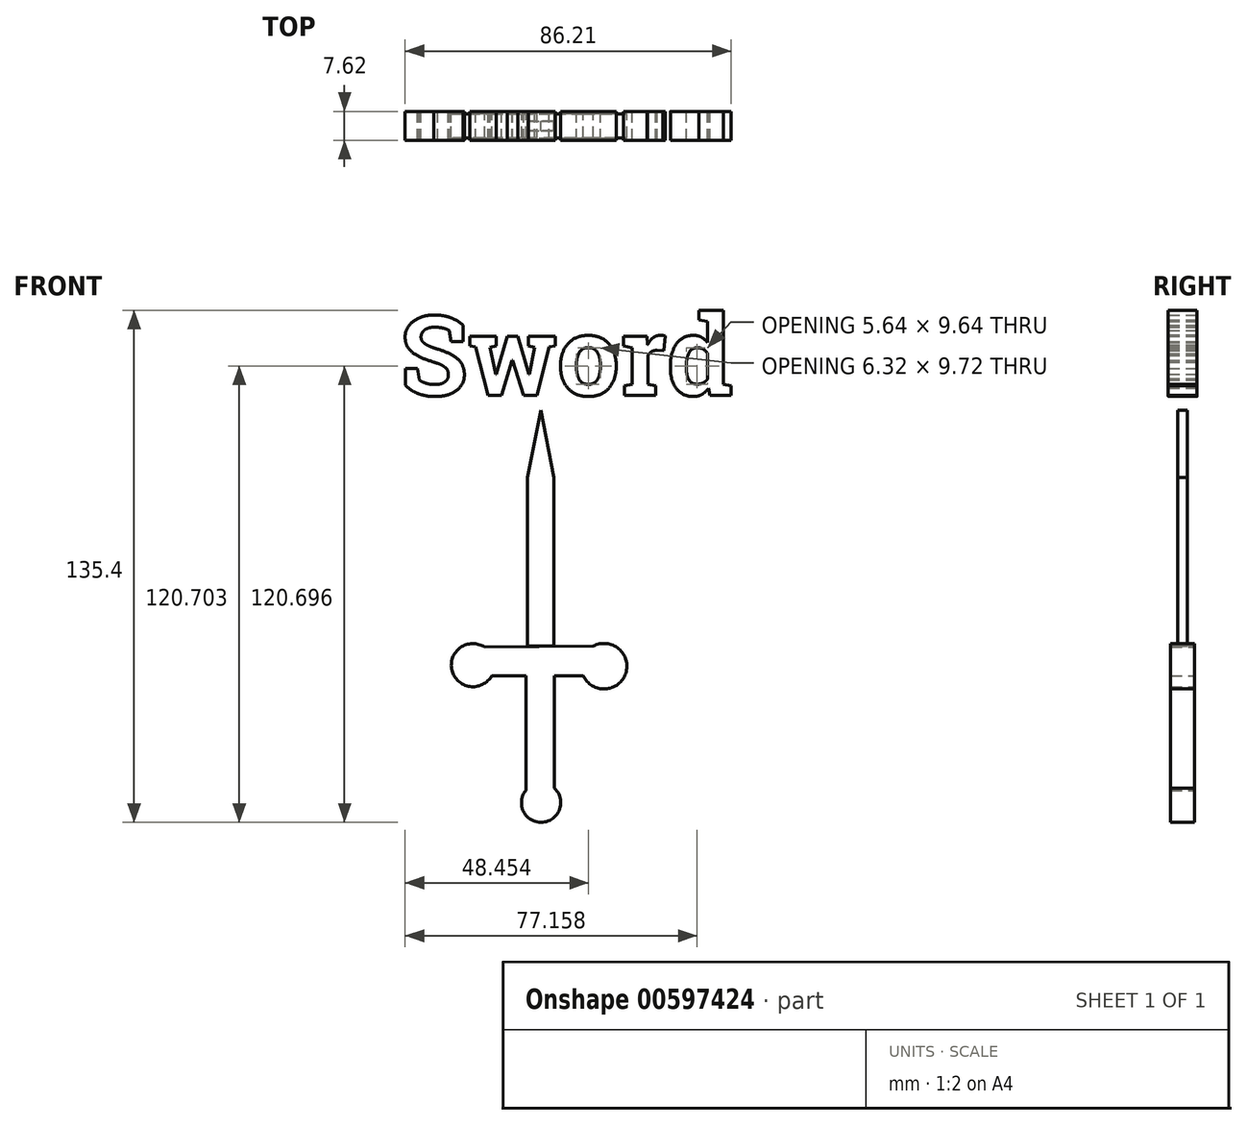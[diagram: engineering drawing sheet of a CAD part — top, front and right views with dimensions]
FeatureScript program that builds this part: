
annotation { "Feature Type Name" : "Feature", "Feature Type Description" : "" }
export const myFeature = defineFeature(function(context is Context, id is Id, definition is map)
    precondition{}
    {
        {
            var Q0;
            Q0=qCreatedBy(makeId("Front.planeOp"),FACE);
            var sketch = newSketch(context, id + "F0", { "sketchPlane" : qUnion([Q0])});
            skLineSegment(sketch, "E0.bottom", {"start": v(-4.06, -25.88) * mm, "end": v(3.5, -25.88) * mm});
            skLineSegment(sketch, "E0.top", {"start": v(-4.06, -56.93) * mm, "end": v(3.5, -56.93) * mm});
            skLineSegment(sketch, "E0.left", {"start": v(-4.06, -25.88) * mm, "end": v(-4.06, -56.93) * mm});
            skLineSegment(sketch, "E0.right", {"start": v(3.5, -25.88) * mm, "end": v(3.5, -56.93) * mm});
            skLineSegment(sketch, "E1", {"start": v(-20, -18.32) * mm, "end": v(-13.85, -25.88) * mm});
            skLineSegment(sketch, "E2", {"start": v(-13.85, -25.88) * mm, "end": v(11.6, -25.88) * mm});
            skPoint(sketch, "E2.endSnap0", {"position": v(-0.28, -25.88) * mm});
            skLineSegment(sketch, "E3", {"start": v(11.6, -25.88) * mm, "end": v(18.04, -18.04) * mm});
            skLineSegment(sketch, "E4", {"start": v(18.04, -18.04) * mm, "end": v(-20, -18.32) * mm});
            skSolve(sketch);
        }
        {
            var Q0;
            Q0 = qSketchRegion(id + "F0", true);
            extrude(context, id + "F1", {"entities" : qUnion([Q0]), "endBound" : BoundingType.SYMMETRIC, "depth" : 6.35 * mm, "offsetDistance" : 25.4 * mm});
        }
        {
            var Q0;
            Q0=qCreatedBy(makeId("Front.planeOp"),FACE);
            var sketch = newSketch(context, id + "F2", { "sketchPlane" : qUnion([Q0])});
            skLineSegment(sketch, "E5", {"start": v(-3.59, -18.05) * mm, "end": v(-3.59, 26.54) * mm});
            skLineSegment(sketch, "E6", {"start": v(-3.59, 26.54) * mm, "end": v(0, 44.34) * mm});
            skLineSegment(sketch, "E7", {"start": v(0, 44.34) * mm, "end": v(3.38, 26.5) * mm});
            skLineSegment(sketch, "E8", {"start": v(3.38, 26.5) * mm, "end": v(3.38, -18.05) * mm});
            skLineSegment(sketch, "E9", {"start": v(3.38, -18.05) * mm, "end": v(-3.59, -18.05) * mm});
            skSolve(sketch);
        }
        {
            var Q0;
            Q0 = qSketchRegion(id + "F2", true);
            extrude(context, id + "F3", {"entities" : qUnion([Q0]), "endBound" : BoundingType.SYMMETRIC, "depth" : 2.54 * mm, "offsetDistance" : 25.4 * mm});
        }
        {
            var Q0;
            Q0=qCreatedBy(makeId("Front.planeOp"),FACE);
            var sketch = newSketch(context, id + "F4", { "sketchPlane" : qUnion([Q0])});
            skCircle(sketch, "E10", {"center": v(0, -59.45) * mm, "radius": 5.2 * mm});
            skSolve(sketch);
        }
        {
            var Q0;
            Q0 = qSketchRegion(id + "F4", true);
            extrude(context, id + "F5", {"entities" : qUnion([Q0]), "operationType" : NewBodyOperationType.ADD, "endBound" : BoundingType.SYMMETRIC, "depth" : 6.35 * mm, "offsetDistance" : 25.4 * mm});
        }
        {
            var Q0;
            Q0=qCreatedBy(makeId("Front.planeOp"),FACE);
            var sketch = newSketch(context, id + "F6", { "sketchPlane" : qUnion([Q0])});
            skCircle(sketch, "E11", {"center": v(16.65, -23.36) * mm, "radius": 6.03 * mm});
            skSolve(sketch);
        }
        {
            var Q0;
            Q0 = qSketchRegion(id + "F6", true);
            extrude(context, id + "F7", {"entities" : qUnion([Q0]), "operationType" : NewBodyOperationType.ADD, "endBound" : BoundingType.SYMMETRIC, "depth" : 6.35 * mm, "offsetDistance" : 25.4 * mm});
        }
        {
            var Q0;
            Q0=qCreatedBy(makeId("Front.planeOp"),FACE);
            var sketch = newSketch(context, id + "F8", { "sketchPlane" : qUnion([Q0])});
            skCircle(sketch, "E12", {"center": v(-18.04, -23.08) * mm, "radius": 5.7 * mm});
            skSolve(sketch);
        }
        {
            var Q0;
            Q0 = qSketchRegion(id + "F8", true);
            extrude(context, id + "F9", {"entities" : qUnion([Q0]), "operationType" : NewBodyOperationType.ADD, "endBound" : BoundingType.SYMMETRIC, "depth" : 6.35 * mm, "offsetDistance" : 25.4 * mm});
        }
        {
            var Q0;
            Q0=qCreatedBy(makeId("Front.planeOp"),FACE);
            var sketch = newSketch(context, id + "F10", { "sketchPlane" : qUnion([Q0])});
            skText(sketch, "E13", { "text": "Sword", "fontName": "RobotoSlab-Bold.ttf"});
            const initialGuessF10  = {"E13": [-0.03735, 0.04826, 1, 0, 0.02126]};
            skSetInitialGuess(sketch, initialGuessF10);
            skSolve(sketch);
        }
        {
            var Q0;
            Q0 = qSketchRegion(id + "F10", true);
            extrude(context, id + "F11", {"entities" : qUnion([Q0]), "endBound" : BoundingType.SYMMETRIC, "depth" : 7.62 * mm, "offsetDistance" : 25.4 * mm});
        }
    });
